FCSTD DOCUMENT  (FreeCAD 1.0R39109 (Git))
Label: powerstripbracket
License: All rights reserved
LicenseURL: http://en.wikipedia.org/wiki/All_rights_reserved
objects: Sketcher::SketchObject×11, PartDesign::Pad×10, PartDesign::SubtractiveCylinder×10, PartDesign::Body×10, PartDesign::AdditiveBox×6, PartDesign::Fillet×5, PartDesign::SubtractiveBox×3, PartDesign::AdditiveCylinder×2, PartDesign::AdditiveCone×2, Part::Feature×1, Mesh::Feature×1
note: 147 computed .brp shape members not serialized (recipe doc carries the construction recipe); baked Part::Feature solids carry a one-line shape summary decoded from their .brp

FEATURE [Sketcher::SketchObject] Sketch
  ArcFitTolerance = 1e-06
  AttachmentSupport = -> [XY_Plane]
  FullyConstrained = true
  MakeInternals = false
  MapMode = 5
  sketch-geometry (8):
    g0: LineSegment StartX=102 StartY=0 StartZ=0 EndX=102 EndY=2 EndZ=0
    g1: LineSegment StartX=7 StartY=2 StartZ=0 EndX=102 EndY=2 EndZ=0
    g2: LineSegment StartX=7 StartY=2 StartZ=0 EndX=7 EndY=7 EndZ=0
    g3: LineSegment StartX=2 StartY=7 StartZ=0 EndX=7 EndY=7 EndZ=0
    g4: LineSegment StartX=2 StartY=7 StartZ=0 EndX=2 EndY=102 EndZ=0
    g5: LineSegment StartX=1.3e-15 StartY=102 StartZ=0 EndX=2 EndY=102 EndZ=0
    g6: LineSegment StartX=1.3e-15 StartY=-1.2e-15 StartZ=0 EndX=1.3e-15 EndY=102 EndZ=0
    g7: LineSegment StartX=0 StartY=0 StartZ=0 EndX=102 EndY=0 EndZ=0
  constraints (24):
    c: Distance(g0) = 2
    c: Vertical(g0)
    c: Distance(g1) = 95
    c: Horizontal(g1)
    c: Distance(g2) = 5
    c: Vertical(g2)
    c: Distance(g3) = 5
    c: Horizontal(g3)
    c: Distance(g4) = 95
    c: Vertical(g4)
    c: Distance(g5) = 2
    c: Horizontal(g5)
    c: Distance(g6) = 102
    c: Vertical(g6)
    c: Distance(g7) = 102
    c: Coincident(g7,g-1)
    c: PointOnObject(g7,g-1)
    c: Coincident(g7,g0)
    c: Coincident(g0,g1)
    c: Coincident(g1,g2)
    c: Coincident(g2,g3)
    c: Coincident(g4,g3)
    c: Coincident(g4,g5)
    c: Coincident(g5,g6)
FEATURE [PartDesign::Pad] Pad
  Direction = (0,0,1)
  Length = 15
  Length2 = 10
  Midplane = true
  Profile = -> Sketch
  ReferenceAxis = -> Sketch [N_Axis]
  Suppressed = false
  Type = 0
FEATURE [PartDesign::SubtractiveCylinder] Cylinder
  Angle = 360
  AttacherType = Attacher::AttachEngine3D
  AttachmentOffset = pos=(94.5,0,-3) rot=(0,0,1;0rad)
  AttachmentSupport = -> [XZ_Plane]
  BaseFeature = -> Pad
  FirstAngle = 0
  Height = 3
  MapMode = 5
  Placement = pos=(94.5,3,-7e-16) rot=(1,0,0;1.5708rad)
  Radius = 2.5
  SecondAngle = 0
  Suppressed = false
FEATURE [PartDesign::SubtractiveCylinder] Cylinder001
  Angle = 360
  AttacherType = Attacher::AttachEngine3D
  AttachmentOffset = pos=(94.5,0,0) rot=(0,0,1;0rad)
  AttachmentSupport = -> [YZ_Plane]
  BaseFeature = -> Cylinder
  FirstAngle = 0
  Height = 3
  MapMode = 5
  Placement = pos=(0,94.5,0) rot=(0.57735,0.57735,0.57735;2.0944rad)
  Radius = 2.5
  SecondAngle = 0
  Suppressed = false
FEATURE [PartDesign::Fillet] Fillet
  Base = -> Cylinder001 [Edge26]
  BaseFeature = -> Cylinder001
  Placement = pos=(0,94.5,0) rot=(0.57735,0.57735,0.57735;2.0944rad)
  Radius = 4.95
  SupportTransform = false
  Suppressed = false
  UseAllEdges = false
FEATURE [PartDesign::Body] Body  label="Bracket"
  AllowCompound = false
  Group = -> [Sketch,Pad,Cylinder,Cylinder001,Fillet]
  Origin = -> Origin
  Placement = pos=(0,0,0) rot=(1,0,0;4.71239rad)
  Tip = -> Fillet
FEATURE [Sketcher::SketchObject] Sketch001
  ArcFitTolerance = 1e-06
  AttachmentSupport = -> [XY_Plane001]
  FullyConstrained = true
  MakeInternals = false
  MapMode = 5
  sketch-geometry (8):
    g0: LineSegment StartX=-0.5 StartY=-8 StartZ=0 EndX=-0.5 EndY=8 EndZ=0
    g1: LineSegment StartX=2.5 StartY=-8 StartZ=0 EndX=2.5 EndY=8 EndZ=0
    g2: LineSegment StartX=-0.5 StartY=8 StartZ=0 EndX=2.5 EndY=8 EndZ=0
    g3: LineSegment StartX=-0.5 StartY=-8 StartZ=0 EndX=2.5 EndY=-8 EndZ=0
    g4: LineSegment StartX=-5.5 StartY=13 StartZ=0 EndX=-5.5 EndY=-13 EndZ=0
    g5: LineSegment StartX=-5.5 StartY=-13 StartZ=0 EndX=7.5 EndY=-13 EndZ=0
    g6: LineSegment StartX=7.5 StartY=-13 StartZ=0 EndX=7.5 EndY=13 EndZ=0
    g7: LineSegment StartX=7.5 StartY=13 StartZ=0 EndX=-5.5 EndY=13 EndZ=0
  constraints (25):
    c: Distance(g0) = 16
    c: Vertical(g0)
    c: Distance(g1) = 16
    c: Vertical(g1)
    c: Distance(g2) = 3
    c: Horizontal(g2)
    c: Distance(g3) = 3
    c: Horizontal(g3)
    c: Distance(g-2,g0) = 0.5
    c: Distance(g0,g-1) = 8
    c: Coincident(g0,g3)
    c: Coincident(g3,g1)
    c: Coincident(g2,g1)
    c: Coincident(g4,g5)
    c: Coincident(g5,g6)
    c: Coincident(g6,g7)
    c: Coincident(g7,g4)
    c: Vertical(g4)
    c: Vertical(g6)
    c: Horizontal(g5)
    c: Horizontal(g7)
    c: Distance(g4,g6) = 13
    c: Distance(g5,g7) = 26
    c: DistanceX(g4,g0) = 5
    c: DistanceY(g4,g0) = 5
FEATURE [PartDesign::Pad] Pad001
  Direction = (0,0,1)
  Length = 66
  Length2 = 10
  Profile = -> Sketch001
  ReferenceAxis = -> Sketch001 [N_Axis]
  Suppressed = false
  Type = 0
FEATURE [PartDesign::SubtractiveBox] Box
  AttacherType = Attacher::AttachEngine3D
  AttachmentOffset = pos=(-8,0,0) rot=(0,0,1;0rad)
  AttachmentSupport = -> [YZ_Plane001]
  BaseFeature = -> Pad001
  Height = 8
  Length = 16
  MapMode = 5
  Placement = pos=(0,-8,0) rot=(0.57735,0.57735,0.57735;2.0944rad)
  Suppressed = false
  Width = 7
FEATURE [PartDesign::AdditiveBox] Box001
  AttacherType = Attacher::AttachEngine3D
  AttachmentOffset = pos=(8,5,-5.5) rot=(0,0,1;0rad)
  AttachmentSupport = -> [YZ_Plane001]
  BaseFeature = -> Box
  Height = 59
  Length = 15
  MapMode = 5
  Placement = pos=(-5.5,8,5) rot=(0.57735,0.57735,0.57735;2.0944rad)
  Suppressed = false
  Width = 5
FEATURE [PartDesign::AdditiveBox] Box002
  AttacherType = Attacher::AttachEngine3D
  AttachmentOffset = pos=(19,0,-5.5) rot=(0,0,1;0rad)
  AttachmentSupport = -> [YZ_Plane001]
  BaseFeature = -> Box001
  Height = 59
  Length = 4
  MapMode = 5
  Placement = pos=(-5.5,19,0) rot=(0.57735,0.57735,0.57735;2.0944rad)
  Suppressed = false
  Width = 5
FEATURE [PartDesign::Body] Body001  label="PowerStrip Holder"
  AllowCompound = false
  Group = -> [Sketch001,Pad001,Box,Box001,Box002]
  Origin = -> Origin001
  Placement = pos=(0,0,0) rot=(1,0,0;3.14159rad)
  Tip = -> Box002
FEATURE [Sketcher::SketchObject] Sketch002
  ArcFitTolerance = 1e-06
  AttachmentSupport = -> [XY_Plane002]
  FullyConstrained = true
  MakeInternals = false
  MapMode = 5
  sketch-geometry (8):
    g0: LineSegment StartX=-0.5 StartY=-8 StartZ=0 EndX=-0.5 EndY=8 EndZ=0
    g1: LineSegment StartX=2.5 StartY=-8 StartZ=0 EndX=2.5 EndY=8 EndZ=0
    g2: LineSegment StartX=-0.5 StartY=8 StartZ=0 EndX=2.5 EndY=8 EndZ=0
    g3: LineSegment StartX=-0.5 StartY=-8 StartZ=0 EndX=2.5 EndY=-8 EndZ=0
    g4: LineSegment StartX=-5.5 StartY=13 StartZ=0 EndX=-5.5 EndY=-13 EndZ=0
    g5: LineSegment StartX=-5.5 StartY=-13 StartZ=0 EndX=7.5 EndY=-13 EndZ=0
    g6: LineSegment StartX=7.5 StartY=-13 StartZ=0 EndX=7.5 EndY=13 EndZ=0
    g7: LineSegment StartX=7.5 StartY=13 StartZ=0 EndX=-5.5 EndY=13 EndZ=0
  constraints (25):
    c: Distance(g0) = 16
    c: Vertical(g0)
    c: Distance(g1) = 16
    c: Vertical(g1)
    c: Distance(g2) = 3
    c: Horizontal(g2)
    c: Distance(g3) = 3
    c: Horizontal(g3)
    c: Distance(g-2,g0) = 0.5
    c: Distance(g0,g-1) = 8
    c: Coincident(g0,g3)
    c: Coincident(g3,g1)
    c: Coincident(g2,g1)
    c: Coincident(g4,g5)
    c: Coincident(g5,g6)
    c: Coincident(g6,g7)
    c: Coincident(g7,g4)
    c: Vertical(g4)
    c: Vertical(g6)
    c: Horizontal(g5)
    c: Horizontal(g7)
    c: Distance(g4,g6) = 13
    c: Distance(g5,g7) = 26
    c: DistanceX(g4,g0) = 5
    c: DistanceY(g4,g0) = 5
FEATURE [PartDesign::Pad] Pad002
  Direction = (0,0,1)
  Length = 36
  Length2 = 10
  Profile = -> Sketch002
  ReferenceAxis = -> Sketch002 [N_Axis]
  Reversed = true
  Suppressed = false
  Type = 0
FEATURE [PartDesign::SubtractiveCylinder] Cylinder002
  Angle = 360
  AttacherType = Attacher::AttachEngine3D
  AttachmentOffset = pos=(0,-28.5,-6) rot=(0,0,1;0rad)
  AttachmentSupport = -> [YZ_Plane002]
  BaseFeature = -> Pad002
  FirstAngle = 0
  Height = 14
  MapMode = 5
  Placement = pos=(-6,0,-28.5) rot=(0.57735,0.57735,0.57735;2.0944rad)
  Radius = 2.5
  SecondAngle = 0
  Suppressed = false
FEATURE [Sketcher::SketchObject] Sketch003
  ArcFitTolerance = 1e-06
  AttachmentSupport = -> [Cylinder002]
  FullyConstrained = true
  MakeInternals = false
  MapMode = 5
  Placement = pos=(-6,0,-36) rot=(0.707107,0.707107,0;3.14159rad)
  sketch-geometry (4):
    g0: LineSegment StartX=-13 StartY=13.5 StartZ=0 EndX=-13 EndY=0.5 EndZ=0
    g1: LineSegment StartX=-13 StartY=0.5 StartZ=0 EndX=13 EndY=0.5 EndZ=0
    g2: LineSegment StartX=13 StartY=0.5 StartZ=0 EndX=13 EndY=13.5 EndZ=0
    g3: LineSegment StartX=13 StartY=13.5 StartZ=0 EndX=-13 EndY=13.5 EndZ=0
  constraints (12):
    c: Coincident(g0,g1)
    c: Coincident(g1,g2)
    c: Coincident(g2,g3)
    c: Coincident(g3,g0)
    c: Vertical(g0)
    c: Vertical(g2)
    c: Horizontal(g1)
    c: Horizontal(g3)
    c: Distance(g0,g2) = 26
    c: Distance(g1,g3) = 13
    c: Distance(g2,g-1) = 13.5
    c: Distance(g1,g-2) = 13
FEATURE [PartDesign::Pad] Pad003
  BaseFeature = -> Cylinder002
  Direction = (0,0,-1)
  Length = 90
  Length2 = 10
  Placement = pos=(-6,0,-28.5) rot=(0.57735,0.57735,0.57735;2.0944rad)
  Profile = -> Sketch003
  ReferenceAxis = -> Sketch003 [N_Axis]
  Suppressed = false
  Type = 0
FEATURE [Sketcher::SketchObject] Sketch004
  ArcFitTolerance = 1e-06
  AttachmentSupport = -> [Pad003]
  FullyConstrained = true
  MakeInternals = false
  MapMode = 5
  Placement = pos=(-6,0,-126) rot=(0.707107,0.707107,0;3.14159rad)
  sketch-geometry (4):
    g0: LineSegment StartX=-8 StartY=15 StartZ=0 EndX=-8 EndY=-1 EndZ=0
    g1: LineSegment StartX=-8 StartY=-1 StartZ=0 EndX=8 EndY=-1 EndZ=0
    g2: LineSegment StartX=8 StartY=-1 StartZ=0 EndX=8 EndY=15 EndZ=0
    g3: LineSegment StartX=8 StartY=15 StartZ=0 EndX=-8 EndY=15 EndZ=0
  constraints (12):
    c: Coincident(g0,g1)
    c: Coincident(g1,g2)
    c: Coincident(g2,g3)
    c: Coincident(g3,g0)
    c: Vertical(g0)
    c: Vertical(g2)
    c: Horizontal(g1)
    c: Horizontal(g3)
    c: Distance(g0,g2) = 16
    c: Distance(g1,g3) = 16
    c: Distance(g1,g-1) = 1
    c: Distance(g-2,g2) = 8
FEATURE [PartDesign::Pad] Pad004
  BaseFeature = -> Pad003
  Direction = (0,0,-1)
  Length = 8
  Length2 = 10
  Placement = pos=(-6,0,-28.5) rot=(0.57735,0.57735,0.57735;2.0944rad)
  Profile = -> Sketch004
  ReferenceAxis = -> Sketch004 [N_Axis]
  Suppressed = false
  Type = 0
FEATURE [PartDesign::SubtractiveCylinder] Cylinder003
  Angle = 360
  AttacherType = Attacher::AttachEngine3D
  AttachmentOffset = pos=(1,0,-134) rot=(0,0,1;0rad)
  AttachmentSupport = -> [XY_Plane002]
  BaseFeature = -> Pad004
  FirstAngle = 0
  Height = 15
  MapMode = 5
  Placement = pos=(1,0,-134) rot=(0,0,1;0rad)
  Radius = 2
  SecondAngle = 0
  Suppressed = false
FEATURE [PartDesign::Body] Body002  label="Grid Holder"
  AllowCompound = false
  Group = -> [Sketch002,Pad002,Cylinder002,Sketch003,Pad003,Sketch004,Pad004,Cylinder003]
  Origin = -> Origin002
  Placement = pos=(0,0,-66) rot=(0,0,1;0rad)
  Tip = -> Cylinder003
FEATURE [PartDesign::AdditiveCylinder] Cylinder004
  Angle = 360
  AttacherType = Attacher::AttachEngine3D
  AttachmentSupport = -> [XY_Plane003]
  FirstAngle = 0
  Height = 3
  MapMode = 5
  Radius = 14
  SecondAngle = 0
  Suppressed = false
FEATURE [PartDesign::SubtractiveCylinder] Cylinder005
  Angle = 360
  AttacherType = Attacher::AttachEngine3D
  AttachmentSupport = -> [XY_Plane003]
  BaseFeature = -> Cylinder004
  FirstAngle = 0
  Height = 3
  MapMode = 5
  Radius = 2
  SecondAngle = 0
  Suppressed = false
FEATURE [PartDesign::Body] Body003  label="washer"
  AllowCompound = false
  Group = -> [Cylinder004,Cylinder005]
  Origin = -> Origin003
  Placement = pos=(1,0,-202.9) rot=(0,0,1;0rad)
  Tip = -> Cylinder005
FEATURE [Part::Feature] Cable_organizer_003_solid001  label="Cable organizer"
  Placement = pos=(55,96,-1.78e-14) rot=(0.57735,0.57735,0.57735;2.0944rad)
  shape: bbox 15 x 100 x 20 mm, 40710 faces (baked)
FEATURE [Mesh::Feature] Cable_Organizer_6_cables  label="Cable+Organizer+6+cables"
  Placement = pos=(272,155.9,15) rot=(1,0,0;1.5708rad)
FEATURE [PartDesign::AdditiveCylinder] Cylinder006
  Angle = 360
  AttacherType = Attacher::AttachEngine3D
  AttachmentSupport = -> [XY_Plane004]
  FirstAngle = 0
  Height = 192
  MapMode = 5
  Radius = 5
  SecondAngle = 0
  Suppressed = false
FEATURE [PartDesign::AdditiveBox] Box003
  AttacherType = Attacher::AttachEngine3D
  AttachmentOffset = pos=(-5,-5,182) rot=(0,0,1;0rad)
  AttachmentSupport = -> [XY_Plane004]
  BaseFeature = -> Cylinder006
  Height = 5
  Length = 10
  MapMode = 5
  Placement = pos=(-5,-5,182) rot=(0,0,1;0rad)
  Suppressed = false
  Width = 5
FEATURE [PartDesign::AdditiveBox] Box004
  AttacherType = Attacher::AttachEngine3D
  AttachmentOffset = pos=(-5,-5,5) rot=(0,0,1;0rad)
  AttachmentSupport = -> [XY_Plane004]
  BaseFeature = -> Box003
  Height = 5
  Length = 10
  MapMode = 5
  Placement = pos=(-5,-5,5) rot=(0,0,1;0rad)
  Suppressed = false
  Width = 5
FEATURE [PartDesign::SubtractiveCylinder] Cylinder007
  Angle = 360
  AttacherType = Attacher::AttachEngine3D
  AttachmentSupport = -> [XY_Plane004]
  BaseFeature = -> Box004
  FirstAngle = 0
  Height = 10
  MapMode = 5
  Radius = 2
  SecondAngle = 0
  Suppressed = false
FEATURE [PartDesign::SubtractiveCylinder] Cylinder008
  Angle = 360
  AttacherType = Attacher::AttachEngine3D
  AttachmentOffset = pos=(0,0,182) rot=(0,0,1;0rad)
  AttachmentSupport = -> [XY_Plane004]
  BaseFeature = -> Cylinder007
  FirstAngle = 0
  Height = 10
  MapMode = 5
  Placement = pos=(0,0,182) rot=(0,0,1;0rad)
  Radius = 2
  SecondAngle = 0
  Suppressed = false
FEATURE [PartDesign::Body] Body004  label="Pillar"
  AllowCompound = false
  Group = -> [Cylinder006,Box003,Box004,Cylinder007,Cylinder008]
  Origin = -> Origin004
  Placement = pos=(1,-43,-192) rot=(0,0,1;0rad)
  Tip = -> Cylinder008
FEATURE [PartDesign::AdditiveCone] Cone
  Angle = 360
  AttacherType = Attacher::AttachEngine3D
  AttachmentSupport = -> [XY_Plane005]
  Height = 10
  MapMode = 5
  Radius1 = 14
  Radius2 = 9
  Suppressed = false
FEATURE [PartDesign::Fillet] Fillet001
  Base = -> Cone [Edge1]
  BaseFeature = -> Cone
  Radius = 3
  SupportTransform = false
  Suppressed = false
  UseAllEdges = false
FEATURE [PartDesign::SubtractiveBox] Box005
  AttacherType = Attacher::AttachEngine3D
  AttachmentOffset = pos=(-5.2,-5.2,4.8) rot=(0,0,1;0rad)
  AttachmentSupport = -> [XY_Plane005]
  BaseFeature = -> Fillet001
  Height = 5.2
  Length = 10.4
  MapMode = 5
  Placement = pos=(-5.2,-5.2,4.8) rot=(0,0,1;0rad)
  Suppressed = false
  Width = 5.2
FEATURE [PartDesign::AdditiveBox] Box006
  AttacherType = Attacher::AttachEngine3D
  AttachmentOffset = pos=(-8,-8,-8) rot=(0,0,1;0rad)
  AttachmentSupport = -> [XY_Plane005]
  BaseFeature = -> Box005
  Height = 8
  Length = 16
  MapMode = 5
  Placement = pos=(-8,-8,-8) rot=(0,0,1;0rad)
  Suppressed = false
  Width = 16
FEATURE [PartDesign::SubtractiveCylinder] Cylinder009
  Angle = 360
  AttacherType = Attacher::AttachEngine3D
  AttachmentOffset = pos=(0,0,-0.2) rot=(0,0,1;0rad)
  AttachmentSupport = -> [XY_Plane005]
  BaseFeature = -> Box006
  FirstAngle = 0
  Height = 10.2
  MapMode = 5
  Placement = pos=(0,0,-0.2) rot=(0,0,1;0rad)
  Radius = 5.2
  SecondAngle = 0
  Suppressed = false
FEATURE [PartDesign::SubtractiveCylinder] Cylinder010
  Angle = 360
  AttacherType = Attacher::AttachEngine3D
  AttachmentOffset = pos=(0,0,-8) rot=(0,0,1;0rad)
  AttachmentSupport = -> [XY_Plane005]
  BaseFeature = -> Cylinder009
  FirstAngle = 0
  Height = 8
  MapMode = 5
  Placement = pos=(0,0,-8) rot=(0,0,1;0rad)
  Radius = 2
  SecondAngle = 0
  Suppressed = false
FEATURE [PartDesign::Body] Body005  label="Pillar Base"
  AllowCompound = false
  Group = -> [Cone,Fillet001,Box005,Box006,Cylinder009,Cylinder010]
  Origin = -> Origin005
  Placement = pos=(1,-43,-192) rot=(0,0,1;0rad)
  Tip = -> Cylinder010
FEATURE [PartDesign::AdditiveCone] Cone001
  Angle = 360
  AttacherType = Attacher::AttachEngine3D
  AttachmentSupport = -> [XY_Plane006]
  Height = 10
  MapMode = 5
  Radius1 = 10
  Radius2 = 10
  Suppressed = false
FEATURE [PartDesign::Fillet] Fillet002
  Base = -> Cone001 [Edge3]
  BaseFeature = -> Cone001
  Radius = 3
  SupportTransform = false
  Suppressed = false
  UseAllEdges = false
FEATURE [PartDesign::SubtractiveBox] Box007
  AttacherType = Attacher::AttachEngine3D
  AttachmentOffset = pos=(-5.2,-5.2,0) rot=(0,0,1;0rad)
  AttachmentSupport = -> [XY_Plane006]
  BaseFeature = -> Fillet002
  Height = 5.2
  Length = 10.4
  MapMode = 5
  Placement = pos=(-5.2,-5.2,0) rot=(0,0,1;0rad)
  Suppressed = false
  Width = 5.2
FEATURE [PartDesign::AdditiveBox] Box008
  AttacherType = Attacher::AttachEngine3D
  AttachmentOffset = pos=(-20,-5,7) rot=(0,0,1;0rad)
  AttachmentSupport = -> [XY_Plane006]
  BaseFeature = -> Box007
  Height = 3
  Length = 40
  MapMode = 5
  Placement = pos=(-20,-5,7) rot=(0,0,1;0rad)
  Suppressed = false
  Width = 10
FEATURE [PartDesign::SubtractiveCylinder] Cylinder011
  Angle = 360
  AttacherType = Attacher::AttachEngine3D
  AttachmentSupport = -> [XY_Plane006]
  BaseFeature = -> Box008
  FirstAngle = 0
  Height = 10
  MapMode = 5
  Radius = 5.2
  SecondAngle = 0
  Suppressed = false
FEATURE [PartDesign::Body] Body006  label="Pillar Top"
  AllowCompound = false
  Group = -> [Cone001,Fillet002,Box007,Box008,Cylinder011]
  Origin = -> Origin006
  Placement = pos=(1,-43,-10) rot=(0,0,1;0rad)
  Tip = -> Cylinder011
FEATURE [Sketcher::SketchObject] Sketch005
  ArcFitTolerance = 1e-06
  AttachmentSupport = -> [XY_Plane007]
  FullyConstrained = true
  MakeInternals = false
  MapMode = 5
  sketch-geometry (48):
    g0: LineSegment StartX=-100 StartY=20 StartZ=0 EndX=-100 EndY=-20 EndZ=0
    g1: LineSegment StartX=-100 StartY=-20 StartZ=0 EndX=108 EndY=-20 EndZ=0
    g2: LineSegment StartX=108 StartY=-20 StartZ=0 EndX=108 EndY=20 EndZ=0
    g3: LineSegment StartX=108 StartY=20 StartZ=0 EndX=-100 EndY=20 EndZ=0
    g4: Circle CenterX=8.1 CenterY=-8.9 CenterZ=0 NormalX=0 NormalY=0 NormalZ=1 AngleXU=0 Radius=3.1
    g5: Circle CenterX=40.3 CenterY=-8.9 CenterZ=0 NormalX=0 NormalY=0 NormalZ=1 AngleXU=0 Radius=3.1
    g6: LineSegment StartX=93.75 StartY=10 StartZ=0 EndX=90.875 EndY=14.9796 EndZ=0
    g7: LineSegment StartX=90.875 StartY=14.9796 StartZ=0 EndX=85.125 EndY=14.9796 EndZ=0
    g8: LineSegment StartX=85.125 StartY=14.9796 StartZ=0 EndX=82.25 EndY=10 EndZ=0
    g9: LineSegment StartX=82.25 StartY=10 StartZ=0 EndX=85.125 EndY=5.02035 EndZ=0
    g10: LineSegment StartX=85.125 StartY=5.02035 StartZ=0 EndX=90.875 EndY=5.02035 EndZ=0
    g11: LineSegment StartX=90.875 StartY=5.02035 StartZ=0 EndX=93.75 EndY=10 EndZ=0
    g12: Circle [constr] CenterX=88 CenterY=10 CenterZ=0 NormalX=0 NormalY=0 NormalZ=1 AngleXU=0 Radius=5.75
    g13: LineSegment StartX=93.75 StartY=-10 StartZ=0 EndX=90.875 EndY=-5.02035 EndZ=0
    g14: LineSegment StartX=90.875 StartY=-5.02035 StartZ=0 EndX=85.125 EndY=-5.02035 EndZ=0
    g15: LineSegment StartX=85.125 StartY=-5.02035 StartZ=0 EndX=82.25 EndY=-10 EndZ=0
    g16: LineSegment StartX=82.25 StartY=-10 StartZ=0 EndX=85.125 EndY=-14.9796 EndZ=0
    g17: LineSegment StartX=85.125 StartY=-14.9796 StartZ=0 EndX=90.875 EndY=-14.9796 EndZ=0
    g18: LineSegment StartX=90.875 StartY=-14.9796 StartZ=0 EndX=93.75 EndY=-10 EndZ=0
    g19: Circle [constr] CenterX=88 CenterY=-10 CenterZ=0 NormalX=0 NormalY=0 NormalZ=1 AngleXU=0 Radius=5.75
    g20: LineSegment StartX=-74.25 StartY=10 StartZ=0 EndX=-77.125 EndY=14.9796 EndZ=0
    g21: LineSegment StartX=-77.125 StartY=14.9796 StartZ=0 EndX=-82.875 EndY=14.9796 EndZ=0
    g22: LineSegment StartX=-82.875 StartY=14.9796 StartZ=0 EndX=-85.75 EndY=10 EndZ=0
    g23: LineSegment StartX=-85.75 StartY=10 StartZ=0 EndX=-82.875 EndY=5.02035 EndZ=0
    g24: LineSegment StartX=-82.875 StartY=5.02035 StartZ=0 EndX=-77.125 EndY=5.02035 EndZ=0
    g25: LineSegment StartX=-77.125 StartY=5.02035 StartZ=0 EndX=-74.25 EndY=10 EndZ=0
    g26: Circle [constr] CenterX=-80 CenterY=10 CenterZ=0 NormalX=0 NormalY=0 NormalZ=1 AngleXU=0 Radius=5.75
    g27: LineSegment StartX=-74.25 StartY=-10 StartZ=0 EndX=-77.125 EndY=-5.02035 EndZ=0
    g28: LineSegment StartX=-77.125 StartY=-5.02035 StartZ=0 EndX=-82.875 EndY=-5.02035 EndZ=0
    g29: LineSegment StartX=-82.875 StartY=-5.02035 StartZ=0 EndX=-85.75 EndY=-10 EndZ=0
    g30: LineSegment StartX=-85.75 StartY=-10 StartZ=0 EndX=-82.875 EndY=-14.9796 EndZ=0
    g31: LineSegment StartX=-82.875 StartY=-14.9796 StartZ=0 EndX=-77.125 EndY=-14.9796 EndZ=0
    g32: LineSegment StartX=-77.125 StartY=-14.9796 StartZ=0 EndX=-74.25 EndY=-10 EndZ=0
    g33: Circle [constr] CenterX=-80 CenterY=-10 CenterZ=0 NormalX=0 NormalY=0 NormalZ=1 AngleXU=0 Radius=5.75
    g34: LineSegment StartX=-52.75 StartY=-10 StartZ=0 EndX=-55.625 EndY=-5.02035 EndZ=0
    g35: LineSegment StartX=-55.625 StartY=-5.02035 StartZ=0 EndX=-61.375 EndY=-5.02035 EndZ=0
    g36: LineSegment StartX=-61.375 StartY=-5.02035 StartZ=0 EndX=-64.25 EndY=-10 EndZ=0
    g37: LineSegment StartX=-64.25 StartY=-10 StartZ=0 EndX=-61.375 EndY=-14.9796 EndZ=0
    g38: LineSegment StartX=-61.375 StartY=-14.9796 StartZ=0 EndX=-55.625 EndY=-14.9796 EndZ=0
    g39: LineSegment StartX=-55.625 StartY=-14.9796 StartZ=0 EndX=-52.75 EndY=-10 EndZ=0
    g40: Circle [constr] CenterX=-58.5 CenterY=-10 CenterZ=0 NormalX=0 NormalY=0 NormalZ=1 AngleXU=0 Radius=5.75
    g41: LineSegment StartX=72.25 StartY=-10 StartZ=0 EndX=69.375 EndY=-5.02035 EndZ=0
    g42: LineSegment StartX=69.375 StartY=-5.02035 StartZ=0 EndX=63.625 EndY=-5.02035 EndZ=0
    g43: LineSegment StartX=63.625 StartY=-5.02035 StartZ=0 EndX=60.75 EndY=-10 EndZ=0
    g44: LineSegment StartX=60.75 StartY=-10 StartZ=0 EndX=63.625 EndY=-14.9796 EndZ=0
    g45: LineSegment StartX=63.625 StartY=-14.9796 StartZ=0 EndX=69.375 EndY=-14.9796 EndZ=0
    g46: LineSegment StartX=69.375 StartY=-14.9796 StartZ=0 EndX=72.25 EndY=-10 EndZ=0
    g47: Circle [constr] CenterX=66.5 CenterY=-10 CenterZ=0 NormalX=0 NormalY=0 NormalZ=1 AngleXU=0 Radius=5.75
  constraints (120):
    c: Coincident(g0,g1)
    c: Coincident(g1,g2)
    c: Coincident(g2,g3)
    c: Coincident(g3,g0)
    c: Vertical(g0)
    c: Vertical(g2)
    c: Horizontal(g1)
    c: Horizontal(g3)
    c: Distance(g0,g2) = 208
    c: Distance(g1,g3) = 40
    c: Distance(g-1,g3) = 20
    c: Distance(g-2,g0) = 100
    c: Diameter(g4) = 6.2
    c: Diameter(g5) = 6.2
    c: Distance(g4,g0) = 105
    c: Distance(g4,g1) = 8
    c: Distance(g5,g1) = 8
    c: Distance(g4,g5) = 26
    c: Coincident(g6,g7)
    c: Coincident(g7,g8)
    c: Coincident(g8,g9)
    c: Coincident(g9,g10)
    c: Coincident(g10,g11)
    c: Coincident(g11,g6)
    c: Equal(g6, g7-g11) x5
    c: PointOnObject(g6,g12)
    c: PointOnObject(g7,g12)
    c: PointOnObject(g8,g12)
    c: PointOnObject(g9,g12)
    c: PointOnObject(g10,g12)
    c: PointOnObject(g11,g12)
    c: Radius(g12) = 5.75
    c: Distance(g12,g-1) = 10
    c: Parallel(g10,g-1)
    c: Coincident(g13,g14)
    c: Coincident(g14,g15)
    c: Coincident(g15,g16)
    c: Coincident(g16,g17)
    c: Coincident(g17,g18)
    c: Coincident(g18,g13)
    c: Equal(g13, g14-g18) x5
    c: PointOnObject(g13,g19)
    c: PointOnObject(g14,g19)
    c: PointOnObject(g15,g19)
    c: PointOnObject(g16,g19)
    c: PointOnObject(g17,g19)
    c: PointOnObject(g18,g19)
    c: Radius(g19) = 5.75
    c: Distance(g19,g-1) = 10
    c: Parallel(g14,g-1)
    c: Distance(g12,g2) = 20
    c: Distance(g19,g2) = 20
    c: Coincident(g20,g21)
    c: Coincident(g21,g22)
    c: Coincident(g22,g23)
    c: Coincident(g23,g24)
    c: Coincident(g24,g25)
    c: Coincident(g25,g20)
    c: Equal(g20, g21-g25) x5
    c: PointOnObject(g20,g26)
    c: PointOnObject(g21,g26)
    c: PointOnObject(g22,g26)
    c: PointOnObject(g23,g26)
    c: PointOnObject(g24,g26)
    c: PointOnObject(g25,g26)
    c: Radius(g26) = 5.75
    c: Coincident(g27,g28)
    c: Coincident(g28,g29)
    c: Coincident(g29,g30)
    c: Coincident(g30,g31)
    c: Coincident(g31,g32)
    c: Coincident(g32,g27)
    c: Equal(g27, g28-g32) x5
    c: PointOnObject(g27,g33)
    c: PointOnObject(g28,g33)
    c: PointOnObject(g29,g33)
    c: PointOnObject(g30,g33)
    c: PointOnObject(g31,g33)
    c: PointOnObject(g32,g33)
    c: Radius(g33) = 5.75
    c: Parallel(g24,g-1)
    c: Parallel(g28,g-1)
    c: Distance(g33,g0) = 20
    c: Distance(g26,g0) = 20
    c: Distance(g26,g-1) = 10
    c: Distance(g33,g-1) = 10
    c: Coincident(g34,g35)
    c: Coincident(g35,g36)
    c: Coincident(g36,g37)
    c: Coincident(g37,g38)
    c: Coincident(g38,g39)
    c: Coincident(g39,g34)
    c: Equal(g34, g35-g39) x5
    c: PointOnObject(g34,g40)
    c: PointOnObject(g35,g40)
    c: PointOnObject(g36,g40)
    c: PointOnObject(g37,g40)
    c: PointOnObject(g38,g40)
    c: PointOnObject(g39,g40)
    c: Radius(g40) = 5.75
    c: Coincident(g41,g42)
    c: Coincident(g42,g43)
    c: Coincident(g43,g44)
    c: Coincident(g44,g45)
    c: Coincident(g45,g46)
    c: Coincident(g46,g41)
    c: Equal(g41, g42-g46) x5
    c: PointOnObject(g41,g47)
    c: PointOnObject(g42,g47)
    c: PointOnObject(g43,g47)
    c: PointOnObject(g44,g47)
    c: PointOnObject(g45,g47)
    c: PointOnObject(g46,g47)
    c: Radius(g47) = 5.75
    c: Distance(g40,g-1) = 10
    c: Distance(g40,g33) = 10
    c: Parallel(g35,g-1)
    c: Parallel(g42,g-1)
    c: Distance(g47,g-1) = 10
    c: Distance(g47,g19) = 10
FEATURE [PartDesign::Pad] Pad005
  Direction = (0,0,1)
  Length = 5
  Length2 = 10
  Profile = -> Sketch005
  ReferenceAxis = -> Sketch005 [N_Axis]
  Suppressed = false
  Type = 0
FEATURE [Sketcher::SketchObject] Sketch006
  ArcFitTolerance = 1e-06
  AttachmentSupport = -> [Pad005]
  FullyConstrained = true
  MakeInternals = false
  MapMode = 5
  Placement = pos=(0,0,0) rot=(1,0,0;3.14159rad)
  sketch-geometry (4):
    g0: LineSegment StartX=-100 StartY=3 StartZ=0 EndX=-100 EndY=-3 EndZ=0
    g1: LineSegment StartX=-100 StartY=-3 StartZ=0 EndX=108 EndY=-3 EndZ=0
    g2: LineSegment StartX=108 StartY=-3 StartZ=0 EndX=108 EndY=3 EndZ=0
    g3: LineSegment StartX=108 StartY=3 StartZ=0 EndX=-100 EndY=3 EndZ=0
  constraints (12):
    c: Coincident(g0,g1)
    c: Coincident(g1,g2)
    c: Coincident(g2,g3)
    c: Coincident(g3,g0)
    c: Vertical(g0)
    c: Vertical(g2)
    c: Horizontal(g1)
    c: Horizontal(g3)
    c: Distance(g0,g2) = 208
    c: Distance(g1,g3) = 6
    c: Distance(g-1,g3) = 3
    c: Distance(g-1,g0) = 100
FEATURE [PartDesign::Pad] Pad006
  BaseFeature = -> Pad005
  Direction = (0,0,-1)
  Length = 5
  Length2 = 10
  Profile = -> Sketch006
  ReferenceAxis = -> Sketch006 [N_Axis]
  Suppressed = false
  Type = 0
FEATURE [Sketcher::SketchObject] Sketch007
  ArcFitTolerance = 1e-06
  AttachmentSupport = -> [Pad006]
  FullyConstrained = true
  MakeInternals = false
  MapMode = 5
  Placement = pos=(0,0,0) rot=(1,0,0;3.14159rad)
  sketch-geometry (14):
    g0: LineSegment StartX=56.5 StartY=20 StartZ=0 EndX=56.5 EndY=-20 EndZ=0
    g1: LineSegment StartX=56.5 StartY=-20 StartZ=0 EndX=98 EndY=-20 EndZ=0
    g2: LineSegment StartX=98 StartY=-20 StartZ=0 EndX=98 EndY=20 EndZ=0
    g3: LineSegment StartX=98 StartY=20 StartZ=0 EndX=56.5 EndY=20 EndZ=0
    g4: LineSegment StartX=-90 StartY=20 StartZ=0 EndX=-90 EndY=-20 EndZ=0
    g5: LineSegment StartX=-90 StartY=-20 StartZ=0 EndX=-48.5 EndY=-20 EndZ=0
    g6: LineSegment StartX=-48.5 StartY=-20 StartZ=0 EndX=-48.5 EndY=20 EndZ=0
    g7: LineSegment StartX=-48.5 StartY=20 StartZ=0 EndX=-90 EndY=20 EndZ=0
    g8: Circle CenterX=-58.5 CenterY=10 CenterZ=0 NormalX=0 NormalY=0 NormalZ=1 AngleXU=0 Radius=3.2
    g9: Circle CenterX=-80 CenterY=-10 CenterZ=0 NormalX=0 NormalY=0 NormalZ=1 AngleXU=0 Radius=3.2
    g10: Circle CenterX=88 CenterY=10 CenterZ=0 NormalX=0 NormalY=0 NormalZ=1 AngleXU=0 Radius=3.2
    g11: Circle CenterX=88 CenterY=-10 CenterZ=0 NormalX=0 NormalY=0 NormalZ=1 AngleXU=0 Radius=3.2
    g12: Circle CenterX=-80 CenterY=10 CenterZ=0 NormalX=0 NormalY=0 NormalZ=1 AngleXU=0 Radius=3.2
    g13: Circle CenterX=66.5 CenterY=10 CenterZ=0 NormalX=0 NormalY=0 NormalZ=1 AngleXU=0 Radius=3.2
  constraints (42):
    c: Coincident(g0,g1)
    c: Coincident(g1,g2)
    c: Coincident(g2,g3)
    c: Coincident(g3,g0)
    c: Vertical(g0)
    c: Vertical(g2)
    c: Horizontal(g1)
    c: Horizontal(g3)
    c: Distance(g0,g2) = 41.5
    c: Distance(g1,g3) = 40
    c: Distance(g-1,g3) = 20
    c: Distance(g-2,g0) = 56.5
    c: Coincident(g4,g5)
    c: Coincident(g5,g6)
    c: Coincident(g6,g7)
    c: Coincident(g7,g4)
    c: Vertical(g4)
    c: Vertical(g6)
    c: Horizontal(g5)
    c: Horizontal(g7)
    c: Distance(g4,g6) = 41.5
    c: Distance(g5,g7) = 40
    c: Distance(g-1,g7) = 20
    c: Distance(g-2,g6) = 48.5
    c: Diameter(g8) = 6.4
    c: Distance(g8,g-1) = 6.8
    c: Distance(g8,g6) = 6.8
    c: Diameter(g9) = 6.4
    c: Distance(g9,g-1) = 6.8
    c: Diameter(g10) = 6.4
    c: Diameter(g11) = 6.4
    c: Distance(g10,g-1) = 6.8
    c: Distance(g10,g2) = 6.8
    c: Distance(g11,g2) = 6.8
    c: Distance(g11,g-1) = 6.8
    c: Distance(g9,g4) = 6.8
    c: Diameter(g12) = 6.4
    c: Distance(g12,g-1) = 6.8
    c: Distance(g12,g4) = 6.8
    c: Diameter(g13) = 6.4
    c: Distance(g13,g0) = 6.8
    c: Distance(g13,g-1) = 6.8
FEATURE [PartDesign::Pad] Pad007
  BaseFeature = -> Pad006
  Direction = (0,0,-1)
  Length = 5
  Length2 = 10
  Profile = -> Sketch007
  ReferenceAxis = -> Sketch007 [N_Axis]
  Suppressed = false
  Type = 0
FEATURE [PartDesign::Body] Body007  label="Bottom Base"
  AllowCompound = false
  Group = -> [Sketch005,Pad005,Sketch006,Pad006,Sketch007,Pad007]
  Origin = -> Origin007
  Placement = pos=(268,278,0) rot=(0,0,1;0rad)
  Tip = -> Pad007
FEATURE [Sketcher::SketchObject] Sketch010
  ArcFitTolerance = 1e-06
  AttachmentSupport = -> [XY_Plane009]
  FullyConstrained = true
  MakeInternals = false
  MapMode = 5
  sketch-geometry (6):
    g0: LineSegment StartX=-59 StartY=18 StartZ=0 EndX=-59 EndY=-8 EndZ=0
    g1: LineSegment StartX=-59 StartY=-8 StartZ=0 EndX=59 EndY=-8 EndZ=0
    g2: LineSegment StartX=59 StartY=-8 StartZ=0 EndX=59 EndY=18 EndZ=0
    g3: LineSegment StartX=59 StartY=18 StartZ=0 EndX=-59 EndY=18 EndZ=0
    g4: Circle CenterX=4.1 CenterY=11.1 CenterZ=0 NormalX=0 NormalY=0 NormalZ=1 AngleXU=0 Radius=3.1
    g5: Circle CenterX=36.3 CenterY=11.1 CenterZ=0 NormalX=0 NormalY=0 NormalZ=1 AngleXU=0 Radius=3.1
  constraints (18):
    c: Coincident(g0,g1)
    c: Coincident(g1,g2)
    c: Coincident(g2,g3)
    c: Coincident(g3,g0)
    c: Vertical(g0)
    c: Vertical(g2)
    c: Horizontal(g1)
    c: Horizontal(g3)
    c: DistanceX(g3,g3) = 118
    c: Distance(g-1,g3) = 18
    c: DistanceX(g-1,g2) = 59
    c: DistanceY(g0,g0) = 26
    c: Diameter(g4) = 6.2
    c: Distance(g4,g-1) = 8
    c: Distance(g4,g-2) = 1
    c: Diameter(g5) = 6.2
    c: Distance(g5,g4) = 26
    c: Distance(g5,g-1) = 8
FEATURE [PartDesign::Pad] Pad010
  Direction = (0,0,1)
  Length = 5
  Length2 = 10
  Profile = -> Sketch010
  ReferenceAxis = -> Sketch010 [N_Axis]
  Suppressed = false
  Type = 0
FEATURE [Sketcher::SketchObject] Sketch011
  ArcFitTolerance = 1e-06
  AttachmentSupport = -> [Pad010]
  FullyConstrained = true
  MakeInternals = false
  MapMode = 5
  Placement = pos=(0,0,5) rot=(0,0,1;0rad)
  sketch-geometry (4):
    g0: LineSegment StartX=-59 StartY=-4 StartZ=0 EndX=-59 EndY=-8 EndZ=0
    g1: LineSegment StartX=-59 StartY=-8 StartZ=0 EndX=59 EndY=-8 EndZ=0
    g2: LineSegment StartX=59 StartY=-8 StartZ=0 EndX=59 EndY=-4 EndZ=0
    g3: LineSegment StartX=59 StartY=-4 StartZ=0 EndX=-59 EndY=-4 EndZ=0
  constraints (12):
    c: Coincident(g0,g1)
    c: Coincident(g1,g2)
    c: Coincident(g2,g3)
    c: Coincident(g3,g0)
    c: Vertical(g0)
    c: Vertical(g2)
    c: Horizontal(g1)
    c: Horizontal(g3)
    c: DistanceY(g2,g2) = 4
    c: Distance(g-1,g3) = 4
    c: DistanceX(g-1,g2) = 59
    c: DistanceX(g1,g1) = 118
FEATURE [PartDesign::Pad] Pad011
  BaseFeature = -> Pad010
  Direction = (0,0,1)
  Length = 16
  Length2 = 10
  Profile = -> Sketch011
  ReferenceAxis = -> Sketch011 [N_Axis]
  Suppressed = false
  Type = 0
FEATURE [PartDesign::Fillet] Fillet005
  Base = -> Pad011 [Edge10]
  BaseFeature = -> Pad011
  Radius = 4.9
  SupportTransform = false
  Suppressed = false
  UseAllEdges = false
FEATURE [PartDesign::Fillet] Fillet006
  Base = -> Fillet005 [Edge2,Edge11]
  BaseFeature = -> Fillet005
  Radius = 3.9
  SupportTransform = false
  Suppressed = false
  UseAllEdges = false
FEATURE [PartDesign::Body] Body009  label="Cable Holder"
  AllowCompound = false
  Group = -> [Sketch010,Pad010,Sketch011,Pad011,Fillet005,Fillet006]
  Origin = -> Origin009
  Placement = pos=(272,160,0) rot=(0,0,1;0rad)
  Tip = -> Fillet006
FEATURE [Sketcher::SketchObject] Sketch012
  ArcFitTolerance = 1e-06
  AttachmentSupport = -> [XY_Plane010]
  FullyConstrained = true
  MakeInternals = false
  MapMode = 5
  sketch-geometry (7):
    g0: LineSegment StartX=-151 StartY=80 StartZ=0 EndX=-151 EndY=-43 EndZ=0
    g1: LineSegment StartX=-151 StartY=-43 StartZ=0 EndX=57 EndY=-43 EndZ=0
    g2: LineSegment StartX=57 StartY=-43 StartZ=0 EndX=57 EndY=80 EndZ=0
    g3: LineSegment StartX=57 StartY=80 StartZ=0 EndX=-151 EndY=80 EndZ=0
    g4: Circle CenterX=-17.1 CenterY=39.1 CenterZ=0 NormalX=0 NormalY=0 NormalZ=1 AngleXU=0 Radius=3.1
    g5: Circle CenterX=-42.9 CenterY=-32 CenterZ=0 NormalX=0 NormalY=0 NormalZ=1 AngleXU=0 Radius=3.1
    g6: Circle CenterX=-10.7 CenterY=-32 CenterZ=0 NormalX=0 NormalY=0 NormalZ=1 AngleXU=0 Radius=3.1
  constraints (21):
    c: Coincident(g0,g1)
    c: Coincident(g1,g2)
    c: Coincident(g2,g3)
    c: Coincident(g3,g0)
    c: Vertical(g0)
    c: Vertical(g2)
    c: Horizontal(g1)
    c: Horizontal(g3)
    c: DistanceX(g1,g1) = 208
    c: Diameter(g4) = 6.2
    c: DistanceY(g1,g-1) = 43
    c: Distance(g4,g-1) = 36
    c: Distance(g-2,g2) = 57
    c: Distance(g4,g2) = 71
    c: Diameter(g5) = 6.2
    c: Diameter(g6) = 6.2
    c: Distance(g5,g-1) = 28.9
    c: Distance(g6,g-1) = 28.9
    c: Distance(g6,g-2) = 7.6
    c: Distance(g6,g5) = 26
    c: DistanceY(g2,g2) = 123
FEATURE [PartDesign::Body] Body010  label="Base"
  AllowCompound = false
  Group = -> [Sketch012]
  Origin = -> Origin010
  Placement = pos=(319,301.1,0) rot=(0,0,1;0rad)
